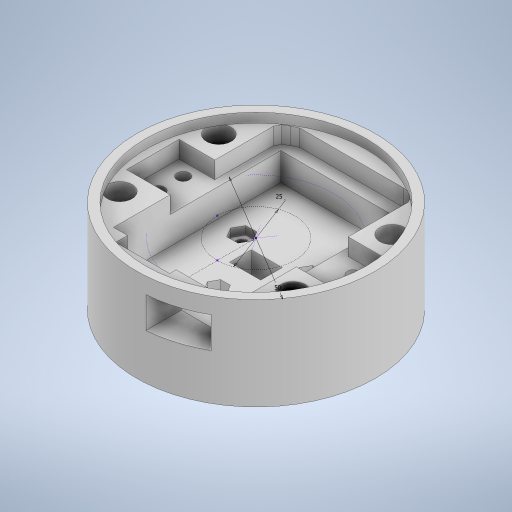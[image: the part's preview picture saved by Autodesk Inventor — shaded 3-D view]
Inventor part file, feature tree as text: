
AUTODESK INVENTOR PART (.ipt)
format: ipt  version: 2024 (Build 280153000, 153)  size: 688,128 bytes
history: native  units: mm
features: sketch x17, extrude x12, hole x1, pattern_circular x1
ambient origin geometry x8: Origin, YZ Plane, XZ Plane, XY Plane, X Axis, Y Axis, Z Axis, Center Point
bodies: Solid1 (feature_tree)
feature tree (31):
  extrude  "Extrusion1"  Depth=20.0mm TaperAngle=0.0deg
  sketch  "Sketch2"  dims[d3=50.0mm d64=25.0mm]
  sketch  "Sketch15"  dims[d70=3.5mm d71=6.0mm d72=4.0mm d73=2.0mm d74=90.0deg d75=8.0mm d76=20.594885mm d77=30.0mm d78=360.0deg]
  hole  "Hole2"  [1 undecoded]
  pattern_circular  "Circular Pattern4"  Count=3 Angle=360.0deg
  extrude  "Extrusion13"  Depth=10.0mm TaperAngle=0.0deg
  extrude  "Extrusion14"  Depth=3.0mm TaperAngle=0.0deg
  extrude  "Extrusion15"  Depth=16.0mm
  extrude  "Extrusion17"  Depth=15.0mm TaperAngle=0.0deg
  sketch  "Sketch32"  dims[d95=38.0mm d96=54.0mm]
  extrude  "Extrusion19"  Depth=54.0mm
  extrude  "Extrusion20"  Depth=4.0mm
  extrude  "Extrusion21"  Depth=11.2mm
  sketch  "Sketch42"  dims[d119=5.4mm d120=3.5mm d121=0.0mm]
  extrude  "Extrusion22"  Depth=0.5mm
  extrude  "Extrusion23"  Depth=3.5mm TaperAngle=0.0deg
  extrude  "Extrusion25"  Depth=2.6mm TaperAngle=0.0deg
  sketch  "Sketch46"  dims[d133=7.0mm]
  extrude  "Extrusion26"  Depth=3.5mm TaperAngle=0.0deg
  sketch  "Sketch1"  dims[d0=77.0mm d1=20.0mm d2=0.0mm]
  sketch  "Sketch27"  dims[d81=77.0mm d82=10.0mm d83=0.0mm]
  sketch  "Sketch28"  dims[d84=71.25mm d85=3.0mm d86=0.0mm]
  sketch  "Sketch29"  dims[d87=28.0mm d88=16.0mm]
  sketch  "Sketch31"  dims[d89=8.0mm d90=15.0mm d91=0.0mm]
  sketch  "Sketch34"  dims[d97=14.5mm d98=0.0mm d105=4.0mm]
  sketch  "Sketch36"  dims[d106=11.2mm d107=0.0mm d108=55.0mm]
  sketch  "Sketch41"  dims[d114=5.5mm d115=0.0mm d117=0.5mm]
  sketch  "Sketch43"  dims[d122=5.4mm d123=2.6mm d124=0.0mm]
  sketch  "Sketch44"  dims[d125=5.4mm d126=3.5mm d127=0.0mm]
  sketch  "Sketch45"  dims[d132=10.0mm]
  sketch  "Sketch47"  dims[d134=0.0mm d135=0.0mm d139=16.1mm d140=10.0mm d141=0.0mm d142=0.0mm d143=4.0mm d12=0.5mm d13=0.872665mm d14=0.5mm d15=0.872665mm d17=0.5mm d18=0.872665mm d19=0.5mm d20=0.872665mm d28=1.0mm d29=1.0mm d30=1.0mm d31=0.15mm d32=0.25mm d33=0.375mm d34=14.3117mm d35=0.75mm d36=20.594885mm d37=0.0625mm d38=0.75mm d39=0.375mm d42=0.5mm d43=0.872665mm d44=0.5mm d45=0.872665mm d144=0.5mm d145=0.872665mm d146=0.5mm d147=0.872665mm]
note: 1 required parameter value undecoded (feature->parameter linkage not recoverable at this tier; creation-order binding heuristic only, values carry confidence <= 0.55)
